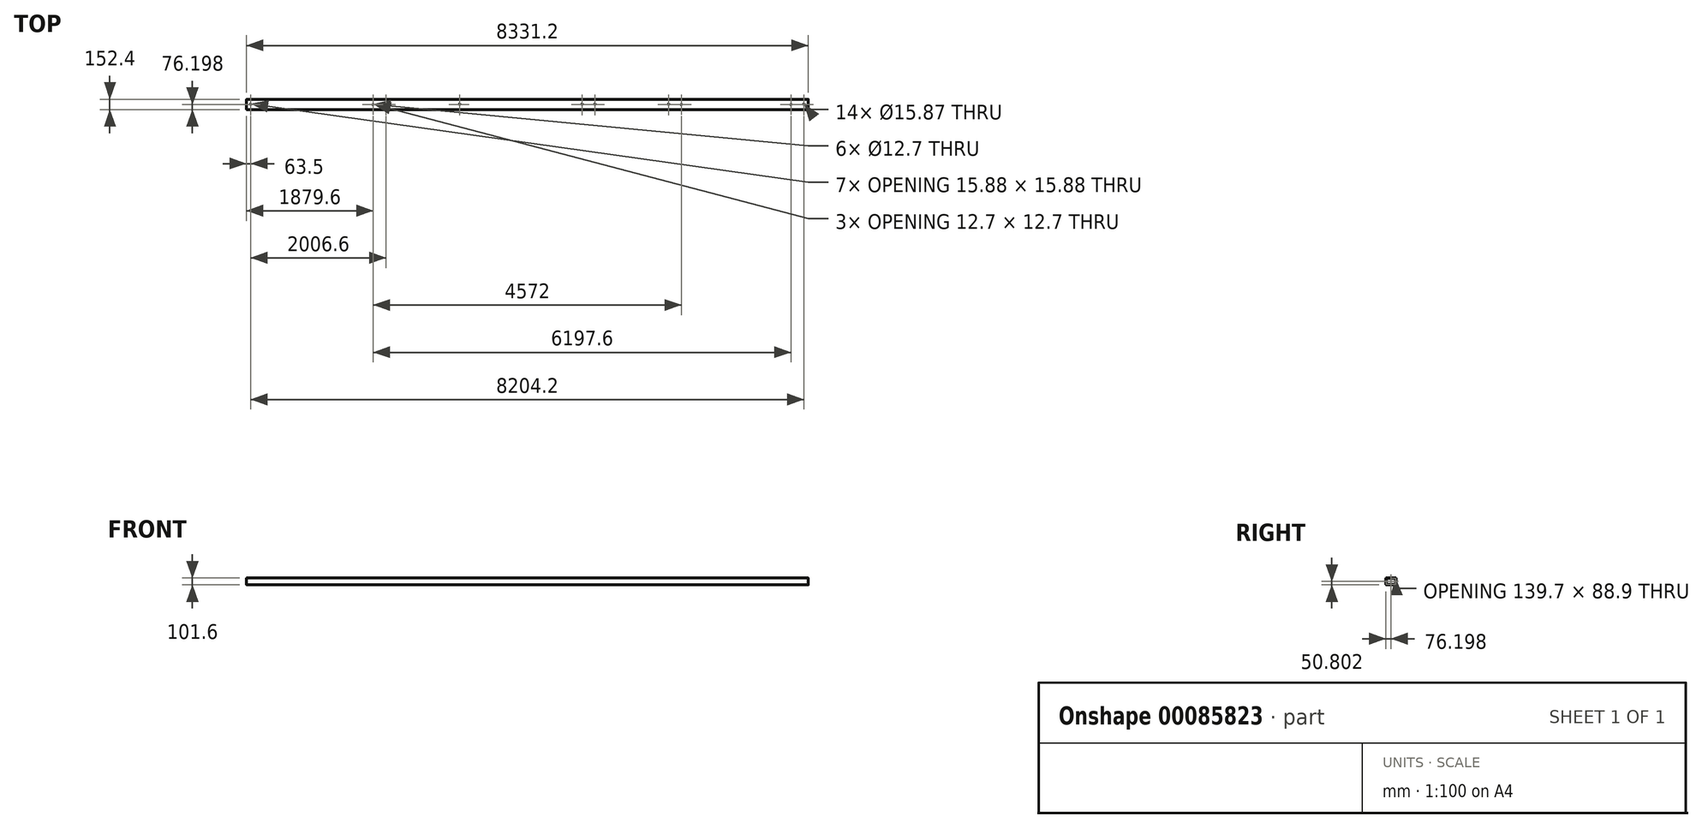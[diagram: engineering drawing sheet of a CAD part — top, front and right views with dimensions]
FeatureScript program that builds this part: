
annotation { "Feature Type Name" : "Feature", "Feature Type Description" : "" }
export const myFeature = defineFeature(function(context is Context, id is Id, definition is map)
    precondition{}
    {
        {
            var Q0;
            Q0=qCreatedBy(makeId("Right.planeOp"),FACE);
            var sketch = newSketch(context, id + "F0", { "sketchPlane" : qUnion([Q0])});
            skLineSegment(sketch, "E0.bottom", {"start": v(56.3, -51.94) * mm, "end": v(-92.96, -51.94) * mm});
            skLineSegment(sketch, "E0.top", {"start": v(56.3, 49.66) * mm, "end": v(-92.96, 49.66) * mm});
            skLineSegment(sketch, "E0.left", {"start": v(57.87, -50.36) * mm, "end": v(57.87, 48.09) * mm});
            skLineSegment(sketch, "E0.right", {"start": v(-94.53, -50.36) * mm, "end": v(-94.53, 48.09) * mm});
            skLineSegment(sketch, "E1.bottom", {"start": v(-86.6, 43.31) * mm, "end": v(49.94, 43.31) * mm});
            skLineSegment(sketch, "E1.top", {"start": v(-86.6, -45.59) * mm, "end": v(49.94, -45.59) * mm});
            skLineSegment(sketch, "E1.left", {"start": v(-88.18, 41.74) * mm, "end": v(-88.18, -44.01) * mm});
            skLineSegment(sketch, "E1.right", {"start": v(51.52, 41.74) * mm, "end": v(51.52, -44.01) * mm});
            skPoint(sketch, "E1.middle", {"position": v(-18.33, -1.14) * mm});
            skPoint(sketch, "E1.middle.positionSnap0", {"position": v(-94.53, -1.14) * mm});
            skPoint(sketch, "E1.middle.positionSnap1", {"position": v(-18.33, 49.66) * mm});
            skPoint(sketch, "E1.centerSnap0", {"position": v(-94.53, -1.14) * mm});
            skPoint(sketch, "E1.centerSnap1", {"position": v(-18.33, 49.66) * mm});
            skPoint(sketch, "E2.visualSharp", {"position": v(-94.53, 49.66) * mm});
            skArc(sketch, "E2.filletArc", {"start": v(-92.96, 49.66) * mm, "mid": v(-94.07, 49.2) * mm, "end": v(-94.53, 48.09) * mm});
            skPoint(sketch, "E3.visualSharp", {"position": v(-88.18, 43.31) * mm});
            skArc(sketch, "E3.filletArc", {"start": v(-86.6, 43.31) * mm, "mid": v(-87.72, 42.85) * mm, "end": v(-88.18, 41.74) * mm});
            skPoint(sketch, "E4.visualSharp", {"position": v(57.87, 49.66) * mm});
            skArc(sketch, "E4.filletArc", {"start": v(57.87, 48.09) * mm, "mid": v(57.4, 49.2) * mm, "end": v(56.3, 49.66) * mm});
            skPoint(sketch, "E5.visualSharp", {"position": v(51.52, 43.31) * mm});
            skArc(sketch, "E5.filletArc", {"start": v(51.52, 41.74) * mm, "mid": v(51.06, 42.85) * mm, "end": v(49.94, 43.31) * mm});
            skPoint(sketch, "E6.visualSharp", {"position": v(57.87, -51.94) * mm});
            skArc(sketch, "E6.filletArc", {"start": v(56.3, -51.94) * mm, "mid": v(57.4, -51.48) * mm, "end": v(57.87, -50.36) * mm});
            skPoint(sketch, "E7.visualSharp", {"position": v(51.52, -45.59) * mm});
            skArc(sketch, "E7.filletArc", {"start": v(49.94, -45.59) * mm, "mid": v(51.06, -45.13) * mm, "end": v(51.52, -44.01) * mm});
            skPoint(sketch, "E8.visualSharp", {"position": v(-88.18, -45.59) * mm});
            skArc(sketch, "E8.filletArc", {"start": v(-88.18, -44.01) * mm, "mid": v(-87.72, -45.13) * mm, "end": v(-86.6, -45.59) * mm});
            skPoint(sketch, "E9.visualSharp", {"position": v(-94.53, -51.94) * mm});
            skArc(sketch, "E9.filletArc", {"start": v(-94.53, -50.36) * mm, "mid": v(-94.07, -51.48) * mm, "end": v(-92.96, -51.94) * mm});
            skSolve(sketch);
        }
        {
            var Q0;
            Q0=makeQuery(id+"F0.imprint","IMPRINT",FACE,{"disambiguationData":[TD([[makeQuery(id+"F0.imprint","IMPRINT",EDGE,{"derivedFrom":sQuery(id+"F0.wireOp",EDGE,"E0.bottom")}),-1.0]])]});
            extrude(context, id + "F1", {"entities" : qUnion([Q0]), "depth" : 8331.2 * mm, "offsetDistance" : 25.4 * mm});
        }
        {
            var Q0;
            Q0=makeQuery(id+"F1.opExtrude","SWEPT_FACE",FACE,{"disambiguationData":[OSD([sQuery(id+"F0.wireOp",EDGE,"E0.bottom")])]});
            var sketch = newSketch(context, id + "F2", { "sketchPlane" : qUnion([Q0])});
            skCircle(sketch, "E10", {"center": v(8077.2, 18.33) * mm, "radius": 6.35 * mm});
            skPoint(sketch, "E10.centerSnap0", {"position": v(8331.2, 18.33) * mm});
            skCircle(sketch, "E11", {"center": v(6451.6, 18.33) * mm, "radius": 6.35 * mm});
            skCircle(sketch, "E12.1.0.0", {"center": v(4978.4, 18.33) * mm, "radius": 6.35 * mm});
            skCircle(sketch, "E12.2.0.0", {"center": v(1879.6, 18.33) * mm, "radius": 6.35 * mm});
            skLineSegment(sketch, "E12.direction1", {"start": v(8077.2, 18.33) * mm, "end": v(4978.4, 18.33) * mm, "construction": true});
            skSolve(sketch);
        }
        {
            var Q0;
            Q0=makeQuery(id+"F2.imprint","IMPRINT",FACE,{"disambiguationData":[TD([[makeQuery(id+"F2.imprint","IMPRINT",EDGE,{"derivedFrom":sQuery(id+"F2.wireOp",EDGE,"E10")}),1.0]])]});
            var Q1;
            Q1=makeQuery(id+"F2.imprint","IMPRINT",FACE,{"disambiguationData":[TD([[makeQuery(id+"F2.imprint","IMPRINT",EDGE,{"derivedFrom":sQuery(id+"F2.wireOp",EDGE,"E11")}),1.0]])]});
            var Q2;
            Q2=makeQuery(id+"F2.imprint","IMPRINT",FACE,{"disambiguationData":[TD([[makeQuery(id+"F2.imprint","IMPRINT",EDGE,{"derivedFrom":sQuery(id+"F2.wireOp",EDGE,"E12.2.0.0")}),1.0]])]});
            extrude(context, id + "F3", {"entities" : qUnion([Q0, Q1, Q2]), "operationType" : NewBodyOperationType.REMOVE, "endBound" : BoundingType.THROUGH_ALL, "oppositeDirection" : true, "depth" : 25.4 * mm, "offsetDistance" : 25.4 * mm});
        }
        {
            var Q0;
            Q0=makeQuery(id+"F1.opExtrude","SWEPT_FACE",FACE,{"disambiguationData":[OSD([sQuery(id+"F0.wireOp",EDGE,"E0.top")])]});
            var sketch = newSketch(context, id + "F4", { "sketchPlane" : qUnion([Q0])});
            skPoint(sketch, "E13", {"position": v(8267.7, -18.33) * mm});
            skPoint(sketch, "E13.positionSnap0", {"position": v(8331.2, -18.33) * mm});
            skPoint(sketch, "E14", {"position": v(6261.1, -18.33) * mm});
            skPoint(sketch, "E15", {"position": v(5168.9, -18.33) * mm});
            skPoint(sketch, "E16", {"position": v(3162.3, -18.33) * mm});
            skPoint(sketch, "E17", {"position": v(2070.1, -18.33) * mm});
            skPoint(sketch, "E18", {"position": v(63.5, -18.33) * mm});
            skSolve(sketch);
        }
        {
            var Q0;
            Q0=sQuery(id+"F4.wireOp",VERTEX,"E14");
            var Q1;
            Q1=sQuery(id+"F4.wireOp",VERTEX,"E13");
            var Q2;
            Q2=sQuery(id+"F4.wireOp",VERTEX,"E16");
            var Q3;
            Q3=sQuery(id+"F4.wireOp",VERTEX,"E17");
            var Q4;
            Q4=sQuery(id+"F4.wireOp",VERTEX,"E18");
            var Q5;
            Q5=sQuery(id+"F4.wireOp",VERTEX,"E15");
            var Q6;
            Q6=sQuery(id+"F2.wireOp",VERTEX,"E12.1.0.0.center");
            var Q7;
            Q7=makeQuery(id+"F1.opExtrude","SWEPT_BODY",BODY,{"disambiguationData":[OSD([sQuery(id+"F0.wireOp",EDGE,"E0.bottom"),sQuery(id+"F0.wireOp",EDGE,"E0.top"),sQuery(id+"F0.wireOp",EDGE,"E0.left"),sQuery(id+"F0.wireOp",EDGE,"E0.right"),sQuery(id+"F0.wireOp",EDGE,"E1.bottom"),sQuery(id+"F0.wireOp",EDGE,"E1.top"),sQuery(id+"F0.wireOp",EDGE,"E1.left"),sQuery(id+"F0.wireOp",EDGE,"E1.right"),sQuery(id+"F0.wireOp",EDGE,"E2.filletArc"),sQuery(id+"F0.wireOp",EDGE,"E3.filletArc"),sQuery(id+"F0.wireOp",EDGE,"E4.filletArc"),sQuery(id+"F0.wireOp",EDGE,"E5.filletArc"),sQuery(id+"F0.wireOp",EDGE,"E6.filletArc"),sQuery(id+"F0.wireOp",EDGE,"E7.filletArc"),sQuery(id+"F0.wireOp",EDGE,"E8.filletArc"),sQuery(id+"F0.wireOp",EDGE,"E9.filletArc")])]});
            hole(context, id + "F5", {"style" : HoleStyle.SIMPLE, "endStyle" : HoleEndStyle.THROUGH, "holeDiameter" : 15.88 * mm, "majorDiameter" : 19.05 * mm, "isTappedThrough" : true, "tappedDepth" : 19.05 * mm, "tapClearance" : 3, "locations" : qUnion([Q0, Q1, Q2, Q3, Q4, Q5, Q6]), "scope" : qUnion([Q7])});
        }
    });
